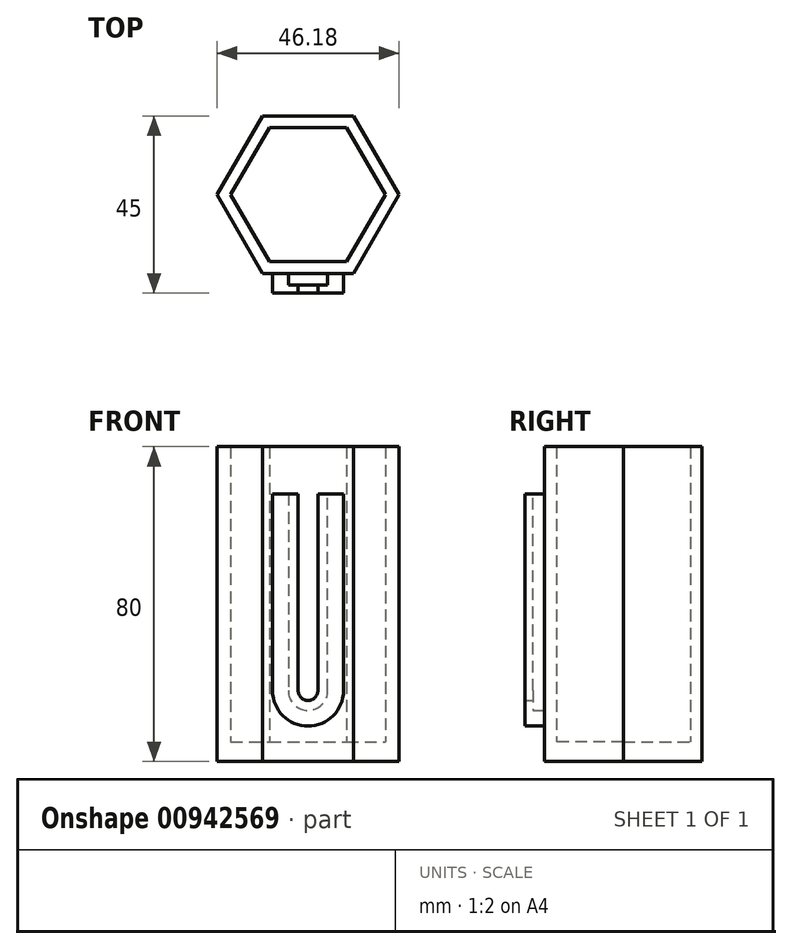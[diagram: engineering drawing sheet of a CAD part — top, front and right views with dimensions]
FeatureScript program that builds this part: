
annotation { "Feature Type Name" : "Feature", "Feature Type Description" : "" }
export const myFeature = defineFeature(function(context is Context, id is Id, definition is map)
    precondition{}
    {
        {
            var Q0;
            Q0=qCreatedBy(makeId("Top.planeOp"),FACE);
            var sketch = newSketch(context, id + "F0", { "sketchPlane" : qUnion([Q0])});
            skCircle(sketch, "E0.cCircle", {"center": v(0, 0) * mm, "radius": 20 * mm, "construction": true});
            skLineSegment(sketch, "E0.0", {"start": v(-11.55, 20) * mm, "end": v(11.55, 20) * mm});
            skLineSegment(sketch, "E0.1", {"start": v(11.55, 20) * mm, "end": v(23.1, 0) * mm});
            skLineSegment(sketch, "E0.2", {"start": v(23.1, 0) * mm, "end": v(11.55, -20) * mm});
            skLineSegment(sketch, "E0.3", {"start": v(11.55, -20) * mm, "end": v(-11.55, -20) * mm});
            skLineSegment(sketch, "E0.4", {"start": v(-11.55, -20) * mm, "end": v(-23.1, 0) * mm});
            skLineSegment(sketch, "E0.5", {"start": v(-23.1, 0) * mm, "end": v(-11.55, 20) * mm});
            skPoint(sketch, "E0.0.midPoint", {"position": v(0, 20) * mm});
            skLineSegment(sketch, "E1.0", {"start": v(-19.63, 0) * mm, "end": v(-9.81, 17) * mm});
            skLineSegment(sketch, "E1.1", {"start": v(9.81, 17) * mm, "end": v(19.63, 0) * mm});
            skLineSegment(sketch, "E1.2", {"start": v(19.63, 0) * mm, "end": v(9.81, -17) * mm});
            skLineSegment(sketch, "E1.3", {"start": v(-9.81, 17) * mm, "end": v(9.81, 17) * mm});
            skLineSegment(sketch, "E1.4", {"start": v(9.81, -17) * mm, "end": v(-9.81, -17) * mm});
            skLineSegment(sketch, "E1.5", {"start": v(-9.81, -17) * mm, "end": v(-19.63, 0) * mm});
            skSolve(sketch);
        }
        {
            var Q0;
            Q0 = qSketchRegion(id + "F0", true);
            extrude(context, id + "F1", {"entities" : qUnion([Q0]), "depth" : 80 * mm, "offsetDistance" : 25.4 * mm});
        }
        {
            var Q0;
            Q0=qCreatedBy(makeId("Top.planeOp"),FACE);
            var sketch = newSketch(context, id + "F2", { "sketchPlane" : qUnion([Q0])});
            skCircle(sketch, "E2.cCircle", {"center": v(0, 0) * mm, "radius": 20 * mm, "construction": true});
            skLineSegment(sketch, "E2.0", {"start": v(-11.55, 20) * mm, "end": v(11.55, 20) * mm});
            skLineSegment(sketch, "E2.1", {"start": v(11.55, 20) * mm, "end": v(23.1, 0) * mm});
            skLineSegment(sketch, "E2.2", {"start": v(23.1, 0) * mm, "end": v(11.55, -20) * mm});
            skLineSegment(sketch, "E2.3", {"start": v(11.55, -20) * mm, "end": v(-11.55, -20) * mm});
            skLineSegment(sketch, "E2.4", {"start": v(-11.55, -20) * mm, "end": v(-23.1, 0) * mm});
            skLineSegment(sketch, "E2.5", {"start": v(-23.1, 0) * mm, "end": v(-11.55, 20) * mm});
            skPoint(sketch, "E2.0.midPoint", {"position": v(0, 20) * mm});
            skSolve(sketch);
        }
        {
            var Q0;
            Q0 = qSketchRegion(id + "F2", true);
            extrude(context, id + "F3", {"entities" : qUnion([Q0]), "operationType" : NewBodyOperationType.ADD, "depth" : 5 * mm, "offsetDistance" : 25 * mm});
        }
        {
            var Q0;
            Q0=makeQuery(id+"F1.opExtrude","SWEPT_FACE",FACE,{"disambiguationData":[OSD([sQuery(id+"F0.wireOp",EDGE,"E0.3")])]});
            var sketch = newSketch(context, id + "F4", { "sketchPlane" : qUnion([Q0])});
            skLineSegment(sketch, "E3", {"start": v(-5, 68) * mm, "end": v(-5, 18) * mm});
            skLineSegment(sketch, "E4", {"start": v(5, 18) * mm, "end": v(5, 68) * mm});
            skArc(sketch, "E5", {"start": v(-5, 18) * mm, "mid": v(0, 13) * mm, "end": v(5, 18) * mm});
            skLineSegment(sketch, "E6.0", {"start": v(9, 18) * mm, "end": v(9, 68) * mm});
            skArc(sketch, "E6.1", {"start": v(-9, 18) * mm, "mid": v(0, 9) * mm, "end": v(9, 18) * mm});
            skLineSegment(sketch, "E6.2", {"start": v(-9, 68) * mm, "end": v(-9, 18) * mm});
            skLineSegment(sketch, "E7", {"start": v(-9, 68) * mm, "end": v(-5, 68) * mm});
            skLineSegment(sketch, "E8", {"start": v(5, 68) * mm, "end": v(9, 68) * mm});
            skSolve(sketch);
        }
        {
            var Q0;
            Q0 = qSketchRegion(id + "F4", true);
            extrude(context, id + "F5", {"entities" : qUnion([Q0]), "operationType" : NewBodyOperationType.ADD, "depth" : 3 * mm, "offsetDistance" : 25 * mm});
        }
        {
            var Q0;
            Q0=makeQuery(id+"F5.opExtrude","CAP_FACE",FACE,{"disambiguationData":[OSD([sQuery(id+"F4.wireOp",EDGE,"E3"),sQuery(id+"F4.wireOp",EDGE,"E4"),sQuery(id+"F4.wireOp",EDGE,"E5"),sQuery(id+"F4.wireOp",EDGE,"E6.0"),sQuery(id+"F4.wireOp",EDGE,"E6.1"),sQuery(id+"F4.wireOp",EDGE,"E6.2"),sQuery(id+"F4.wireOp",EDGE,"E7"),sQuery(id+"F4.wireOp",EDGE,"E8")])],"isStart":false});
            var sketch = newSketch(context, id + "F6", { "sketchPlane" : qUnion([Q0])});
            skLineSegment(sketch, "E9", {"start": v(-9, 68) * mm, "end": v(-9, 18) * mm});
            skLineSegment(sketch, "E10", {"start": v(-9, 68) * mm, "end": v(-2.5, 68) * mm});
            skLineSegment(sketch, "E11", {"start": v(-2.5, 68) * mm, "end": v(-2.5, 18) * mm});
            skLineSegment(sketch, "E12", {"start": v(9, 18) * mm, "end": v(9, 68) * mm});
            skLineSegment(sketch, "E13", {"start": v(9, 68) * mm, "end": v(2.5, 68) * mm});
            skLineSegment(sketch, "E14", {"start": v(2.5, 68) * mm, "end": v(2.5, 18) * mm});
            skArc(sketch, "E15", {"start": v(-2.5, 18) * mm, "mid": v(0, 15.5) * mm, "end": v(2.5, 18) * mm});
            skArc(sketch, "E16", {"start": v(-9, 18) * mm, "mid": v(0, 9) * mm, "end": v(9, 18) * mm});
            skSolve(sketch);
        }
        {
            var Q0;
            Q0 = qSketchRegion(id + "F6", true);
            extrude(context, id + "F7", {"entities" : qUnion([Q0]), "operationType" : NewBodyOperationType.ADD, "depth" : 2 * mm, "offsetDistance" : 25 * mm});
        }
    });
